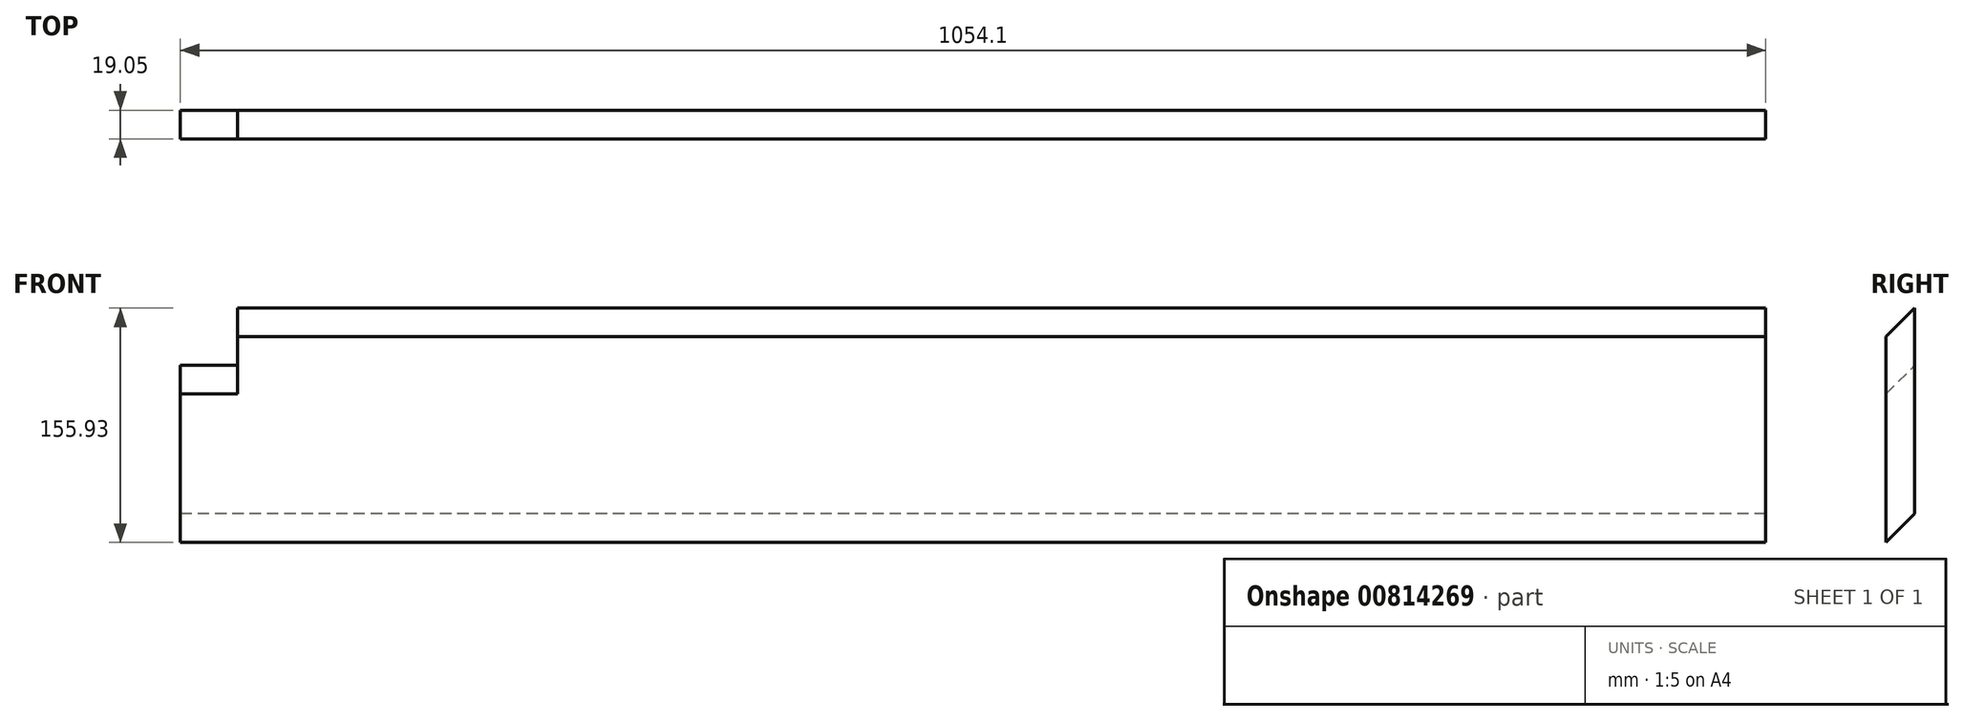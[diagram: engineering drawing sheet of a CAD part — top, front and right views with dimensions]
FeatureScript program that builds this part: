
annotation { "Feature Type Name" : "Feature", "Feature Type Description" : "" }
export const myFeature = defineFeature(function(context is Context, id is Id, definition is map)
    precondition{}
    {
        {
            var Q0;
            Q0=qCreatedBy(makeId("Right.planeOp"),FACE);
            var sketch = newSketch(context, id + "F0", { "sketchPlane" : qUnion([Q0])});
            skLineSegment(sketch, "E0", {"start": v(-19.05, 0) * mm, "end": v(0, 19.05) * mm});
            skLineSegment(sketch, "E1", {"start": v(-19.05, 0) * mm, "end": v(-19.05, 98.78) * mm});
            skLineSegment(sketch, "E2", {"start": v(-19.05, 98.78) * mm, "end": v(0, 117.83) * mm});
            skLineSegment(sketch, "E3", {"start": v(0, 117.83) * mm, "end": v(0, 19.05) * mm});
            skSolve(sketch);
        }
        {
            var Q0;
            Q0 = qSketchRegion(id + "F0", true);
            extrude(context, id + "F1", {"entities" : qUnion([Q0]), "endBound" : BoundingType.SYMMETRIC, "depth" : 1054.1 * mm, "offsetDistance" : 25.4 * mm});
        }
        {
            var Q0;
            Q0=makeQuery(id+"F1.opExtrude","CAP_FACE",FACE,{"disambiguationData":[OSD([sQuery(id+"F0.wireOp",EDGE,"E0"),sQuery(id+"F0.wireOp",EDGE,"E1"),sQuery(id+"F0.wireOp",EDGE,"E2"),sQuery(id+"F0.wireOp",EDGE,"E3")])],"isStart":false});
            var sketch = newSketch(context, id + "F2", { "sketchPlane" : qUnion([Q0])});
            skLineSegment(sketch, "E4", {"start": v(-19.05, 98.78) * mm, "end": v(-19.05, 136.88) * mm});
            skLineSegment(sketch, "E5", {"start": v(0, 117.83) * mm, "end": v(0, 155.93) * mm});
            skLineSegment(sketch, "E6", {"start": v(0, 155.93) * mm, "end": v(-19.05, 136.88) * mm});
            skLineSegment(sketch, "E7", {"start": v(-19.05, 98.78) * mm, "end": v(0, 117.83) * mm});
            skSolve(sketch);
        }
        {
            var Q0;
            Q0 = qSketchRegion(id + "F2", true);
            extrude(context, id + "F3", {"entities" : qUnion([Q0]), "operationType" : NewBodyOperationType.ADD, "oppositeDirection" : true, "depth" : 1016 * mm, "offsetDistance" : 25.4 * mm});
        }
    });
